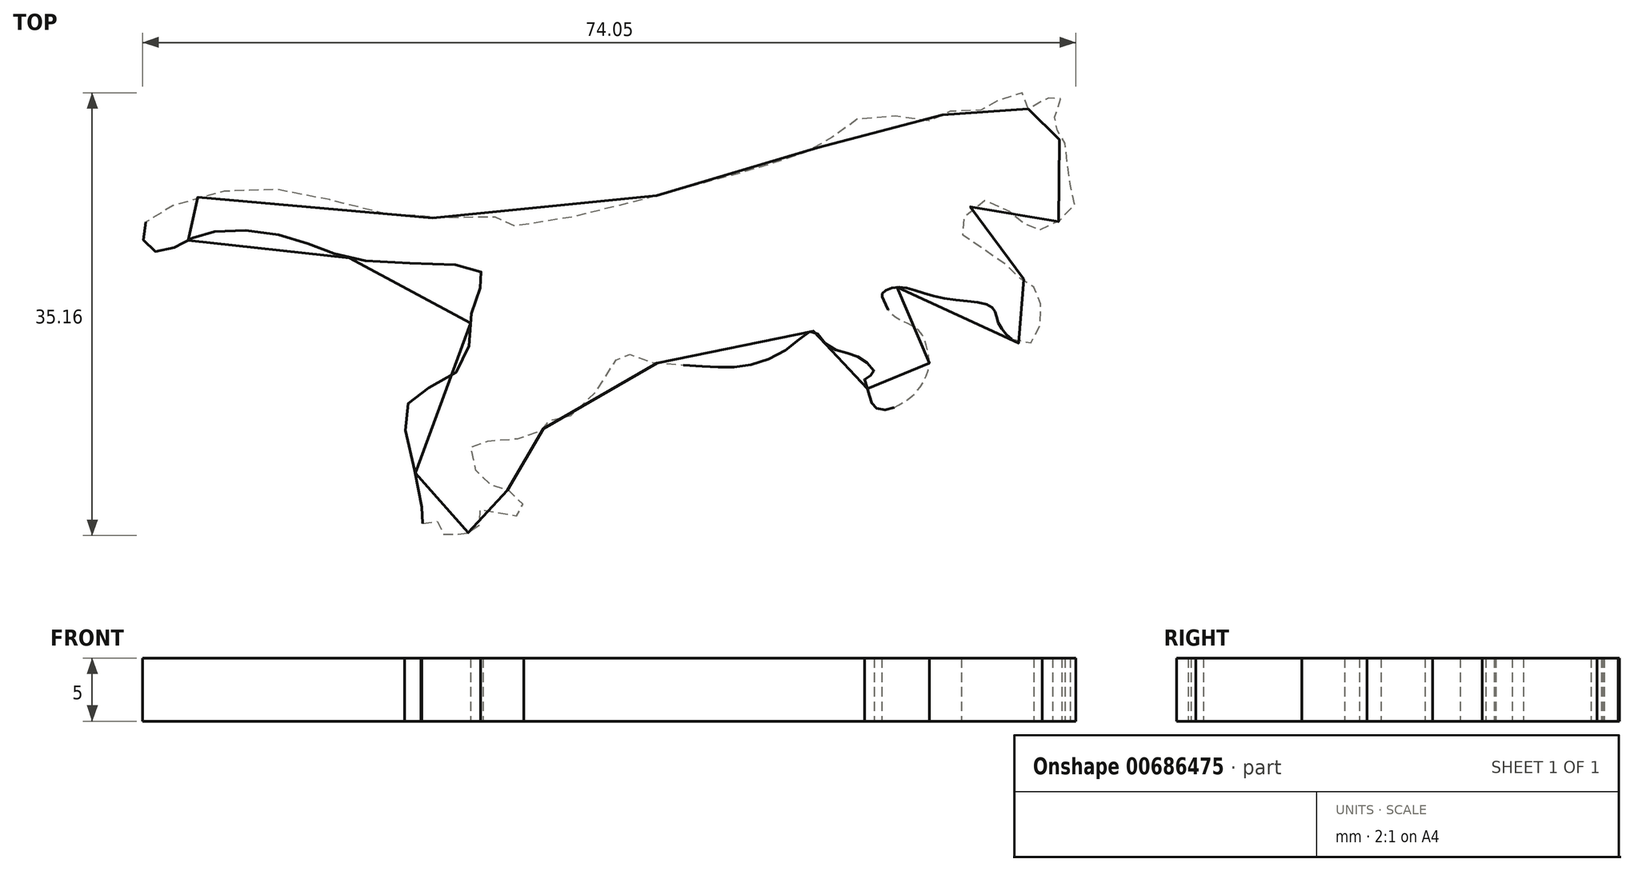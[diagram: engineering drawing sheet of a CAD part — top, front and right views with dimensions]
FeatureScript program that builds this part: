
annotation { "Feature Type Name" : "Feature", "Feature Type Description" : "" }
export const myFeature = defineFeature(function(context is Context, id is Id, definition is map)
    precondition{}
    {
        {
            var Q0;
            Q0=qCreatedBy(makeId("Top.planeOp"),FACE);
            var sketch = newSketch(context, id + "F0", { "sketchPlane" : qUnion([Q0])});
            skFitSpline(sketch, "E0", {"points": [v(-4.85, 43.58) * mm, v(-5.08, 44.62) * mm, v(-5.43, 44.85) * mm, v(-7.23, 44.27) * mm, v(-7.81, 43.46) * mm, v(-9.79, 43.63) * mm, v(-11.82, 43) * mm, v(-12.86, 42.59) * mm, v(-16.12, 43.05) * mm, v(-19.31, 42.3) * mm, v(-20.94, 40.85) * mm, v(-23.67, 39.74) * mm, v(-26.69, 38.75) * mm, v(-28.84, 38.17) * mm, v(-36.1, 36.2) * mm, v(-46.2, 34.34) * mm, v(-46.79, 34.86) * mm, v(-53.35, 34.92) * mm, v(-61.3, 36.6) * mm, v(-68.4, 37.07) * mm, v(-74.15, 35.21) * mm, v(-75.08, 34.17) * mm, v(-74.84, 32.6) * mm, v(-73.57, 32.25) * mm, v(-71.77, 33) * mm, v(-69.85, 33.76) * mm, v(-65.32, 33.76) * mm, v(-61.2, 32.54) * mm, v(-56.9, 31.44) * mm, v(-48.76, 30.91) * mm, v(-48.12, 30.1) * mm, v(-49, 27.6) * mm, v(-49.75, 23.19) * mm, v(-53.35, 20.92) * mm, v(-54.34, 18.54) * mm, v(-53, 11.86) * mm, v(-52.94, 10.64) * mm, v(-51.78, 10.81) * mm, v(-51.38, 9.88) * mm, v(-50.56, 9.71) * mm, v(-49.87, 9.83) * mm, v(-49.17, 9.94) * mm, v(-48.36, 10.64) * mm, v(-48.36, 11.74) * mm, v(-47.43, 11.63) * mm, v(-45.16, 11.34) * mm, v(-45.04, 12.38) * mm, v(-46.73, 13.49) * mm, v(-48.24, 14.18) * mm, v(-49.05, 16.74) * mm, v(-47.02, 17.2) * mm, v(-43.42, 18.08) * mm, v(-42.95, 18.77) * mm, v(-40.57, 19.53) * mm, v(-37.03, 24.17) * mm, v(-35.98, 23.77) * mm, v(-31.51, 23.19) * mm, v(-28.02, 23.07) * mm, v(-24.02, 24.46) * mm, v(-21.93, 25.92) * mm, v(-20.76, 24.76) * mm, v(-19.02, 24.12) * mm, v(-17.69, 23.42) * mm, v(-17.1, 22.55) * mm, v(-17.8, 22.2) * mm, v(-17.69, 21.5) * mm, v(-17.4, 20.57) * mm, v(-17.1, 19.93) * mm, v(-16.3, 19.64) * mm, v(-15.13, 20.05) * mm, v(-13.74, 21.1) * mm, v(-12.75, 23.01) * mm, v(-12.86, 24.4) * mm, v(-13.56, 25.98) * mm, v(-15.65, 27.2) * mm, v(-16.3, 28.3) * mm, v(-16.47, 28.82) * mm, v(-15.25, 29.4) * mm, v(-11.93, 28.59) * mm, v(-7.75, 27.83) * mm, v(-7.29, 26.73) * mm, v(-6, 25.16) * mm, v(-4.85, 24.87) * mm, v(-4.2, 25.63) * mm, v(-3.8, 26.85) * mm, v(-3.86, 28.07) * mm, v(-4.38, 28.7) * mm, v(-4.5, 29.93) * mm, v(-5.43, 30.04) * mm, v(-6.07, 30.56) * mm, v(-7.7, 32.07) * mm, v(-9.67, 33.12) * mm, v(-10.13, 33.76) * mm, v(-10.02, 34.75) * mm, v(-8.68, 36.31) * mm, v(-6.6, 35.5) * mm, v(-5.9, 35.27) * mm, v(-4.96, 34.22) * mm, v(-4.32, 34) * mm, v(-3.1, 34.1) * mm, v(-1.89, 35.21) * mm, v(-1.13, 36.08) * mm, v(-1.36, 37.3) * mm, v(-1.94, 38.7) * mm, v(-1.54, 40.2) * mm, v(-2.06, 40.9) * mm, v(-2.47, 41.25) * mm, v(-2.64, 42.18) * mm, v(-2.93, 42.47) * mm, v(-2.3, 43.63) * mm, v(-2.3, 44.39) * mm, v(-2.87, 44.74) * mm, v(-3.45, 44.21) * mm, v(-4.85, 43.58) * mm]});
            skSolve(sketch);
        }
        {
            var Q0;
            Q0 = qSketchRegion(id + "F0", true);
            extrude(context, id + "F1", {"entities" : qUnion([Q0]), "depth" : 5 * mm, "offsetDistance" : 25.4 * mm});
        }
    });
